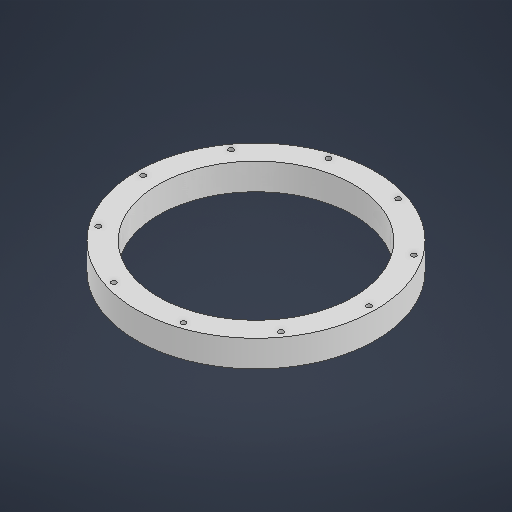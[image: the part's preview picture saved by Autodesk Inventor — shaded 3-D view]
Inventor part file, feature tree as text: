
AUTODESK INVENTOR PART (.ipt)
format: ipt  version: 2025 (Build 290162000, 162)  size: 243,200 bytes
history: native  units: in
note: dims shown in document units (in); Inventor stores cm internally (conversion verified against a paired STEP export)
features: sketch x9, extrude x6, hole x1
ambient origin geometry x8: Origin, YZ Plane, XZ Plane, XY Plane, X Axis, Y Axis, Z Axis, Center Point
bodies: Solid1 (feature_tree)
feature tree (16):
  extrude  "Extrusion1"  Depth=8.6614in
  hole  "Hole1"  [1 undecoded]
  extrude  "Extrusion7"  Depth=3.937in TaperAngle=360.0deg
  extrude  "Extrusion8"  Depth=0.3937in
  extrude  "Extrusion9"  Depth=0.3937in TaperAngle=0.0deg
  extrude  "Extrusion10"  Depth=5.1181in
  extrude  "Extrusion11"  Depth=5.9055in
  sketch  "Sketch1"  dims[d0=10.6299in d1=8.6614in]
  sketch  "Sketch3"  dims[d9=0.1575in d10=3.937in d12=360.0deg]
  sketch  "Sketch Circular Pattern1"  dims[d2=1.1811in d3=0.0in d8=10.0394in]
  sketch  "Sketch8"  dims[d37=0.3937in d38=0.0in d39=0.1969in d40=0.0in]
  sketch  "Sketch9"  dims[d41=8.6614in d42=5.1181in]
  sketch  "Sketch10"  dims[d43=0.0984in d44=0.0in d45=5.9055in]
  sketch  "Sketch11"  dims[d46=6.0236in]
  sketch  "Sketch12"  dims[d47=0.0197in d48=0.0in d49=6.6929in d55=0.2165in d56=2.3622in d58=360.0deg d60=0.0197in d61=0.0in d24=0.0197in d25=0.0344in d26=0.0197in d27=0.0344in d30=0.0197in d31=0.0344in d32=0.0197in d33=0.0344in d34=0.0197in d35=0.0344in]
  sketch  "Sketch Circular Pattern3"  dims[d14=0.2165in d15=0.3937in d16=0.1575in d17=0.0787in d18=90.0deg d19=0.315in d20=0.8108in d36=4.9213in]
note: 1 required parameter value undecoded (feature->parameter linkage not recoverable at this tier; creation-order binding heuristic only, values carry confidence <= 0.55)
